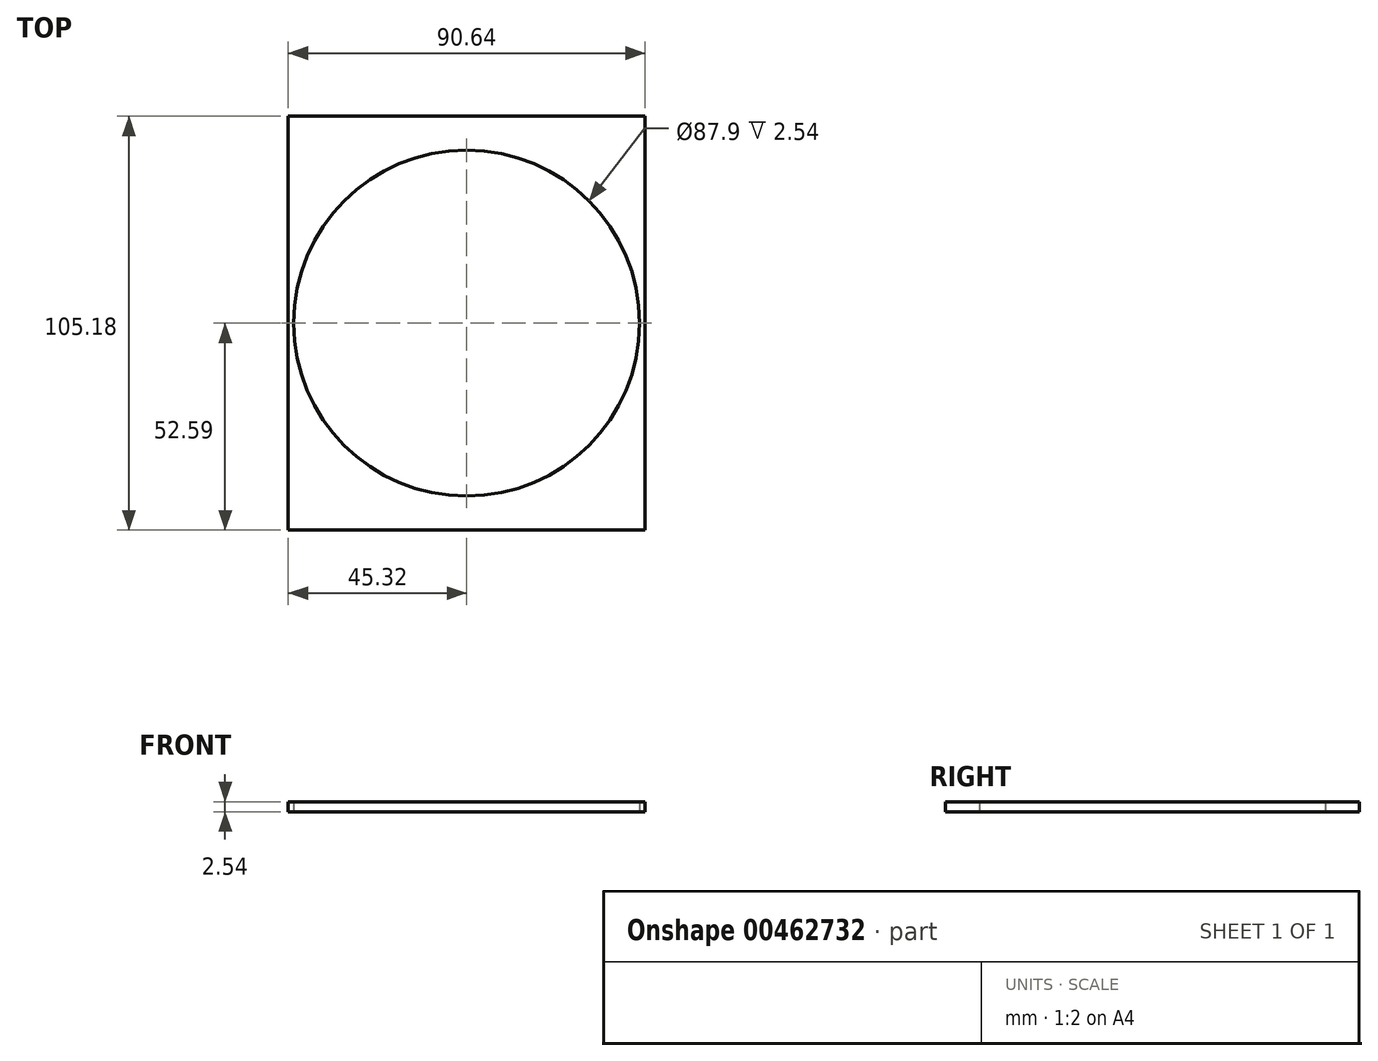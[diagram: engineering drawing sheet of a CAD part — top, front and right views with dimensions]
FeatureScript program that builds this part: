
annotation { "Feature Type Name" : "Feature", "Feature Type Description" : "" }
export const myFeature = defineFeature(function(context is Context, id is Id, definition is map)
    precondition{}
    {
        {
            var Q0;
            Q0=qCreatedBy(makeId("Top.planeOp"),FACE);
            var sketch = newSketch(context, id + "F0", { "sketchPlane" : qUnion([Q0])});
            skLineSegment(sketch, "E0.bottom", {"start": v(45.32, 52.6) * mm, "end": v(-45.32, 52.6) * mm});
            skLineSegment(sketch, "E0.top", {"start": v(45.32, -52.6) * mm, "end": v(-45.32, -52.6) * mm});
            skLineSegment(sketch, "E0.left", {"start": v(45.32, 52.6) * mm, "end": v(45.32, -52.6) * mm});
            skLineSegment(sketch, "E0.right", {"start": v(-45.32, 52.6) * mm, "end": v(-45.32, -52.6) * mm});
            skPoint(sketch, "E0.middle", {"position": v(0, 0) * mm});
            skCircle(sketch, "E1", {"center": v(0, 0) * mm, "radius": 43.95 * mm});
            skSolve(sketch);
        }
        {
            var Q0;
            Q0=makeQuery(id+"F0.imprint","IMPRINT",FACE,{"disambiguationData":[TD([[makeQuery(id+"F0.imprint","IMPRINT",EDGE,{"derivedFrom":sQuery(id+"F0.wireOp",EDGE,"E0.bottom")}),1.0]])]});
            extrude(context, id + "F1", {"entities" : qUnion([Q0]), "depth" : 2.54 * mm});
        }
    });
